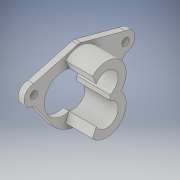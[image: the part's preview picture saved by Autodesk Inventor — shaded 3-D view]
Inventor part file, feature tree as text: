
AUTODESK INVENTOR PART (.ipt)
format: ipt  version: 2017 (Build 210142000, 142)  size: 174,592 bytes
history: native  units: in
note: dims shown in document units (in); Inventor stores cm internally (conversion verified against a paired STEP export)
features: extrude x2, sketch x2, fillet x1, projected_geometry x1
ambient origin geometry x8: Origin, YZ Plane, XZ Plane, XY Plane, X Axis, Y Axis, Z Axis, Center Point
bodies: Solid1 (feature_tree)
feature tree (6):
  extrude  "Extrusion1"  Depth=0.2756in
  fillet  "Fillet1"  Radius=0.475in
  extrude  "Extrusion4"  Depth=0.557in
  sketch  "Sketch1"  dims[d0=0.475in d1=0.2756in d2=0.475in]
  sketch  "Sketch4"  dims[d3=0.2756in d5=1.4567in d6=0.8in d7=0.3285in d8=0.146in d11=0.146in d14=0.396in d15=0.396in d26=0.4002in d27=0.125in d28=0.0in d29=0.125in d39=0.81in d40=0.81in d41=0.557in d42=0.0in]
  projected_geometry  "Projected Loop3"
